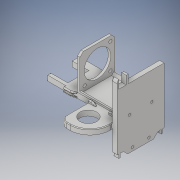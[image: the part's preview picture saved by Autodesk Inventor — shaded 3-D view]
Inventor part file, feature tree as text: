
AUTODESK INVENTOR PART (.ipt)
format: ipt  version: 2019.4 (Build 234330000, 330)  size: 1,011,200 bytes
history: native  units: mm
features: other x35, extrude x14, fillet x11, loft x6, sketch x5, move_body x4, mirror x2, projected_geometry x2, imported_body x2, boolean_combine x1
ambient origin geometry x8: Origin, YZ Plane, XZ Plane, XY Plane, X Axis, Y Axis, Z Axis, Center Point
bodies: Solid1 (feature_tree), Solid2 (feature_tree), Solid3 (feature_tree), Solid5 (feature_tree), Solid8 (feature_tree), Solid7 (feature_tree), Solid9 (feature_tree)
feature tree (82):
  other  "Repaired Geometry2"
  other  "Repaired Geometry3"
  extrude  "Base Extrusion (6.2)"  Depth=10.0mm
  extrude  "Base Screw Counterbore (3.3 | 5.4)"  Depth=2.6mm
  other  "Platform Plane"
  extrude  "Platform Extrusion (6.2)"  Depth=5.4mm
  extrude  "Extruder Divider Plane"  Depth=5.4mm
  extrude  "Extruder Divider Extrusion (3)"  Depth=0.79mm TaperAngle=0.0deg
  fillet  "Sensor Rear Fillet (24)"  [1 undecoded]
  fillet  "Sensor Front Fillet (8)"  Radius=82.75mm
  extrude  "Sensor Extursion (Through)"  Depth=0.79mm
  extrude  "Outer Extrusion Rail (47)"  Depth=0.79mm
  other  "Outer Triangle Rail Sketch"
  other  "Top Base Plane"
  loft  "Rail Angled Loft"
  extrude  "Inner Rail Extrusion"  Depth=0.79mm
  extrude  "Fan Screw Holes Extrude (3.2)"  Depth=0.79mm
  other  "Top Wire Holder Plane"
  extrude  "Top Wire Holder Extrusion"  Depth=0.79mm
  other  "Wire Holder Second Plane"
  other  "Second Top Wireholder Sketch"
  other  "Second Bottom Wireholder Sketch"
  loft  "Wireholder Second Top Loft"
  loft  "Wireholder Second Bottom Loft"
  other  "Third Wireholder Plane"
  loft  "Third Wireholder Top Loft"
  other  "Wireholder Half Plane"
  mirror  "Third Wireholder Bottom Loft"
  other  "Second Wireholder Plane"
  other  "Platform Mirror Plane"
  mirror  "Second Wireholder Solid"
  move_body  "Move Body1"
  fillet  "Sensor Fillet (.8)"  Radius=4.0mm
  fillet  "Big Wire Holder Outside Fillet (4)"  Radius=47.0mm
  fillet  "Base Trim Fillet (.8)"  Radius=32.107684mm
  fillet  "Extruder Motor Support Fillet (.8)"  Radius=6.2mm
  fillet  "Small Base Trim Fillet (.8)"  [1 undecoded]
  fillet  "Bottom Base Trim Left Fillet (.8)"  Radius=3.0mm
  move_body  "Move Body2"
  fillet  "Extruder Inner Motor Support Fillet (.8)"  Radius=24.0mm
  fillet  "Top Base Trim Fillet (.8)"  Radius=8.0mm
  other  "Top Sensor Wire Holder Plane"
  extrude  "Sensor Front Wire Holder Extrusion (3)"  Depth=0.79mm
  other  "Sensor Wire Holder Second Plane"
  other  "Sensor Wire Holder Second Sketch"
  other  "Sensor Wire Holder Third Plane"
  other  "Sensor Wire Holder Third Sketch"
  loft  "Sensor Wire Holder First Loft"
  loft  "Sensor Wire Holder Second Loft"
  move_body  "Move Body3"
  other  "Vertical Base Wire Holder Plane"
  extrude  "Outer Vertical Wire Holder Extrusion (8)"  Depth=0.79mm TaperAngle=0.0deg
  move_body  "Move Body4"
  other  "Horizontal Base Wire Holder Plane"
  extrude  "Horizontal Base Wire Holder Extrusion (8)"  Depth=0.79mm TaperAngle=0.0deg
  boolean_combine  "Combine1"
  fillet  "Small Base Trim Inner Fillet (.8)"  [1 undecoded]
  other  "Base Sketch"
  sketch  "Sketch2"  dims[d3=10.0mm d4=2.0mm]
  other  "Platform Sketch"
  extrude  "Extruder Divider Sketch"  TaperAngle=0.0deg  [1 undecoded]
  other  "Sensor Sketch (20)"
  sketch  "Sketch6"  dims[d5=10.8mm d6=2.6mm]
  projected_geometry  "Projected Loop1"
  other  "Base Triangle Rail Sketch"
  other  "Edges1"
  other  "Inner Rail Sketch"
  other  "Fan Hole Sketch"
  other  "Wire Holder Top Sketch"
  other  "Edges2"
  other  "Edges3"
  other  "Third Wireholder Top Sketch"
  other  "Edges4"
  other  "Pattern of Solid2:1"
  sketch  "Sketch15"  dims[d7=6.2mm d8=0.0mm d9=5.4mm]
  other  "Edges7"
  other  "Edges8"
  imported_body  "Base2"
  sketch  "Sketch18"  dims[d12=5.4mm d13=5.4mm]
  imported_body  "Base3"
  sketch  "Sketch20"  dims[d14=5.4mm d15=3.3mm d16=0.0mm d17=-29.0mm d18=82.75mm d19=35.85mm d20=37.8mm d21=53.52mm d22=4.0mm d23=20.9mm d24=25.45mm d25=20.9mm d26=8.55mm d27=36.52mm d28=4.0mm d29=47.0mm d30=32.107684mm d31=6.2mm d32=0.0mm d33=0.0mm d34=3.0mm d35=0.0mm d36=24.0mm d37=8.0mm d38=15.0mm d39=18.9mm d40=20.0mm d41=3.0mm d42=0.0mm d43=47.0mm d44=0.0mm d45=0.0mm d46=0.0mm d47=90.0deg d48=0.0mm d49=90.0deg d50=0.0mm d51=90.0deg d52=47.0mm d53=0.0mm d54=4.0mm d55=28.0mm d56=2.8mm d57=1.5mm d58=3.2mm d59=0.0mm d60=-22.8mm d61=3.0mm d62=2.0mm d63=0.4mm d64=0.6mm d65=8.0mm d66=0.0mm d67=-11.0mm d68=0.4mm d70=0.0mm d71=90.0deg d72=0.0mm d73=90.0deg d74=0.0mm d75=90.0deg d76=0.0mm d77=90.0deg d78=0.0mm d79=90.0deg d80=2.2mm d81=0.0mm d82=90.0deg d83=0.0mm d84=90.0deg d85=-3.1mm d86=-8.3mm d87=-21.0mm d88=22.02mm d89=0.0mm d90=0.0mm d91=0.8mm d92=4.0mm d93=0.8mm d94=0.8mm d95=0.8mm d96=0.8mm d97=0.0mm d98=0.8mm d99=0.0mm d100=0.8mm d101=0.8mm d102=-0.8mm d108=3.0mm d109=0.0mm d110=3.0mm d111=0.4mm d121=0.0mm d122=90.0deg d123=0.0mm d124=90.0deg d125=0.0mm d126=90.0deg d127=0.0mm d128=90.0deg d129=24.0mm d130=0.0mm d131=0.0mm d132=-27.6mm d133=1.93mm d139=5.53mm d140=8.0mm d141=0.0mm d142=0.0mm d143=0.0mm d144=43.6mm d149=-20.0mm d150=5.76mm d151=1.93mm d152=5.53mm d153=8.0mm d154=0.0mm d155=0.79mm]
  projected_geometry  "Projected Loop2"
note: 4 required parameter values undecoded (feature->parameter linkage not recoverable at this tier; creation-order binding heuristic only, values carry confidence <= 0.55)
